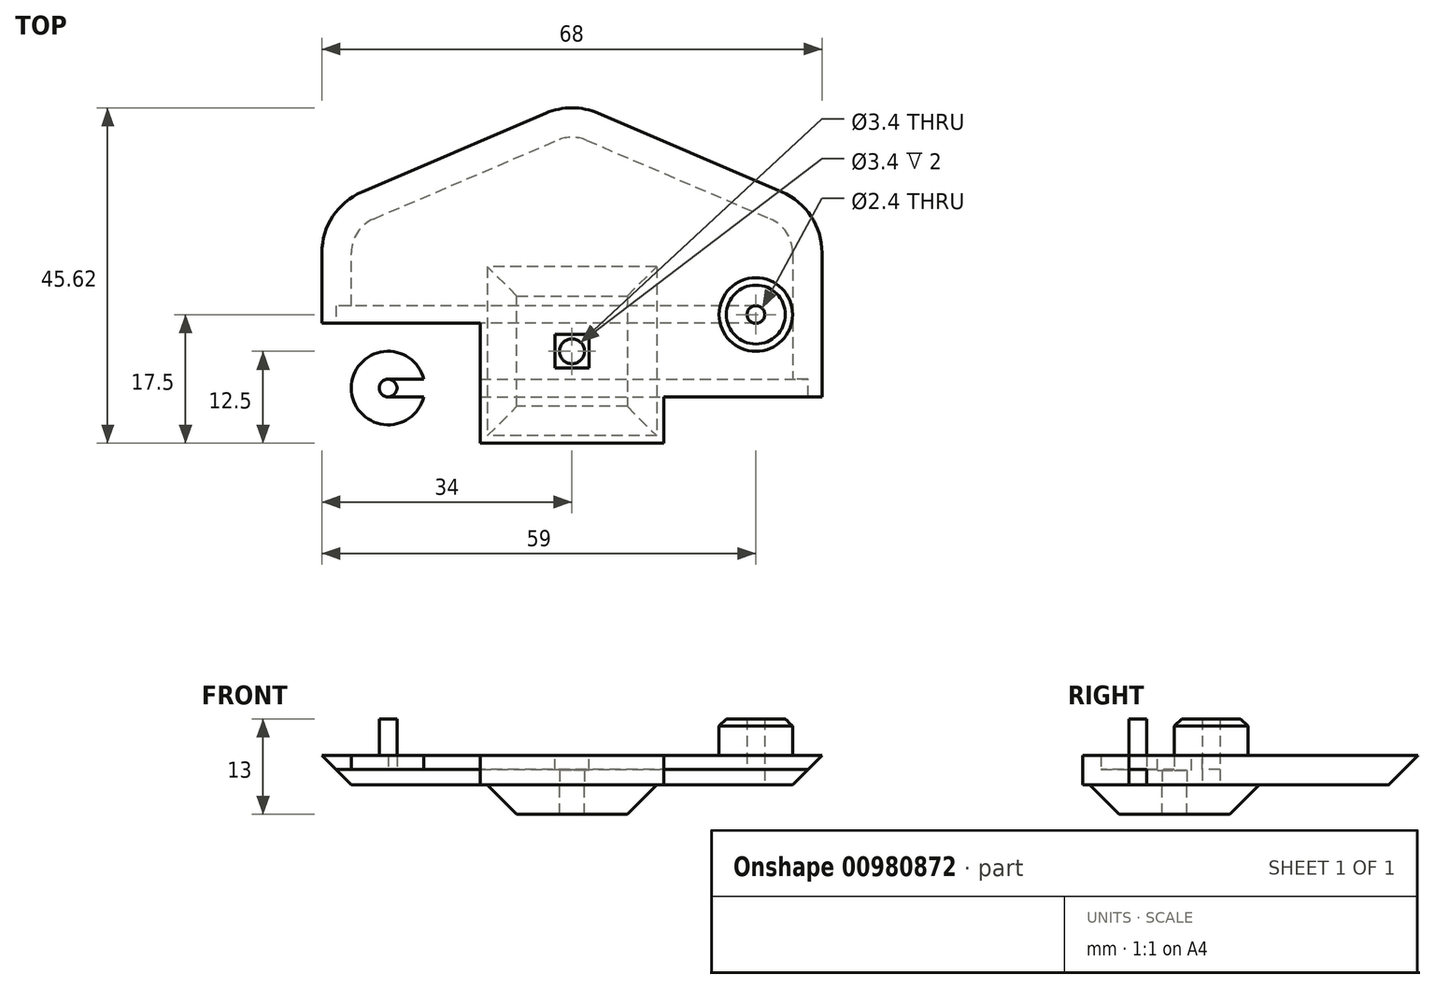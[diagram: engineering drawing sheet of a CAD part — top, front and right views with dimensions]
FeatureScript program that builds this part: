
annotation { "Feature Type Name" : "Feature", "Feature Type Description" : "" }
export const myFeature = defineFeature(function(context is Context, id is Id, definition is map)
    precondition{}
    {
        {
            var Q0;
            Q0=qCreatedBy(makeId("Top.planeOp"),FACE);
            var sketch = newSketch(context, id + "F0", { "sketchPlane" : qUnion([Q0])});
            skLineSegment(sketch, "E0.bottom", {"start": v(35, 35) * mm, "end": v(-35, 35) * mm, "construction": true});
            skLineSegment(sketch, "E0.left", {"start": v(35, 35) * mm, "end": v(35, 20) * mm, "construction": true});
            skLineSegment(sketch, "E0.right", {"start": v(-35, 35) * mm, "end": v(-35, 20) * mm, "construction": true});
            skPoint(sketch, "E0.middle", {"position": v(0, 0) * mm});
            skCircle(sketch, "E1", {"center": v(25, 5) * mm, "radius": 5 * mm});
            skLineSegment(sketch, "E2", {"start": v(35, 20) * mm, "end": v(-35, 20) * mm, "construction": true});
            skLineSegment(sketch, "E3", {"start": v(28.94, 22.6) * mm, "end": v(3.94, 33.31) * mm});
            skLineSegment(sketch, "E4", {"start": v(-3.94, 33.31) * mm, "end": v(-28.94, 22.6) * mm});
            skPoint(sketch, "E5.visualSharp", {"position": v(0, 35) * mm});
            skArc(sketch, "E5.filletArc", {"start": v(3.94, 33.31) * mm, "mid": v(0, 34.12) * mm, "end": v(-3.94, 33.31) * mm});
            skLineSegment(sketch, "E6", {"start": v(35, 13.4) * mm, "end": v(35, 0.5) * mm});
            skLineSegment(sketch, "E7", {"start": v(-35, 13.4) * mm, "end": v(-35, 0.3) * mm});
            skPoint(sketch, "E8.visualSharp", {"position": v(35, 20) * mm});
            skArc(sketch, "E8.filletArc", {"start": v(35, 13.4) * mm, "mid": v(33.35, 18.91) * mm, "end": v(28.94, 22.6) * mm});
            skPoint(sketch, "E9.visualSharp", {"position": v(-35, 20) * mm});
            skArc(sketch, "E9.filletArc", {"start": v(-28.94, 22.6) * mm, "mid": v(-33.35, 18.91) * mm, "end": v(-35, 13.4) * mm});
            skPoint(sketch, "E0.top.end.orphan", {"position": v(-35, -35) * mm});
            skPoint(sketch, "E10.end.orphan", {"position": v(35, -35) * mm});
            skCircle(sketch, "E11.MirrorC", {"center": v(25, 5) * mm, "radius": 1.2 * mm});
            skArc(sketch, "E12.MirrorCS", {"start": v(3.94, -33.31) * mm, "mid": v(0, -34.12) * mm, "end": v(-3.94, -33.31) * mm});
            skArc(sketch, "E13.MirrorCS", {"start": v(-28.94, -22.6) * mm, "mid": v(-33.35, -18.91) * mm, "end": v(-35, -13.4) * mm});
            skPoint(sketch, "E14.MirrorP", {"position": v(-35, -20) * mm});
            skArc(sketch, "E15.MirrorCS", {"start": v(35, -13.4) * mm, "mid": v(33.35, -18.91) * mm, "end": v(28.94, -22.6) * mm});
            skLineSegment(sketch, "E16.MirrorCS", {"start": v(28.94, -22.6) * mm, "end": v(3.94, -33.31) * mm});
            skLineSegment(sketch, "E17.MirrorCS", {"start": v(35, -35) * mm, "end": v(35, -20) * mm, "construction": true});
            skLineSegment(sketch, "E18.MirrorCS", {"start": v(35, -20) * mm, "end": v(-35, -20) * mm, "construction": true});
            skLineSegment(sketch, "E19.MirrorCS", {"start": v(35, -35) * mm, "end": v(-35, -35) * mm, "construction": true});
            skLineSegment(sketch, "E20.MirrorCS", {"start": v(-35, -35) * mm, "end": v(-35, -20) * mm, "construction": true});
            skLineSegment(sketch, "E21.MirrorCS", {"start": v(35, -13.4) * mm, "end": v(35, -0.5) * mm});
            skPoint(sketch, "E22.MirrorP", {"position": v(0, -35) * mm});
            skPoint(sketch, "E23.MirrorP", {"position": v(35, -20) * mm});
            skLineSegment(sketch, "E24.MirrorCS", {"start": v(-3.94, -33.31) * mm, "end": v(-28.94, -22.6) * mm});
            skLineSegment(sketch, "E25.MirrorCS", {"start": v(-35, -13.4) * mm, "end": v(-35, -0.3) * mm});
            skCircle(sketch, "E26.MirrorC", {"center": v(-25, -5) * mm, "radius": 1.2 * mm});
            skCircle(sketch, "E27.MirrorC", {"center": v(-25, -5) * mm, "radius": 5 * mm});
            skLineSegment(sketch, "E28.bottom", {"start": v(12.5, 12.5) * mm, "end": v(-12.5, 12.5) * mm});
            skLineSegment(sketch, "E28.top", {"start": v(12.5, -12.5) * mm, "end": v(-12.5, -12.5) * mm});
            skLineSegment(sketch, "E28.left", {"start": v(12.5, 12.5) * mm, "end": v(12.5, -12.5) * mm});
            skLineSegment(sketch, "E28.right", {"start": v(-12.5, 12.5) * mm, "end": v(-12.5, -12.5) * mm});
            skCircle(sketch, "E29", {"center": v(0, 0) * mm, "radius": 1.7 * mm});
            skLineSegment(sketch, "E30", {"start": v(-35, -0.3) * mm, "end": v(-35, 0.3) * mm});
            skLineSegment(sketch, "E31", {"start": v(35, -0.5) * mm, "end": v(35, 0.5) * mm});
            skLineSegment(sketch, "E32", {"start": v(25, 3.8) * mm, "end": v(-35, 3.8) * mm});
            skPoint(sketch, "E32.endSnap0", {"position": v(-35, 6.85) * mm});
            skLineSegment(sketch, "E33", {"start": v(25, 6.2) * mm, "end": v(-35, 6.2) * mm});
            skLineSegment(sketch, "E34", {"start": v(-25, -6.2) * mm, "end": v(35, -6.2) * mm});
            skLineSegment(sketch, "E35", {"start": v(-25, -3.8) * mm, "end": v(35, -3.8) * mm});
            skSolve(sketch);
        }
        {
            var Q0;
            Q0=makeQuery(id+"F0.imprint","IMPRINT",FACE,{"disambiguationData":[TD([[makeQuery(id+"F0.imprint","IMPRINT",EDGE,{"derivedFrom":sQuery(id+"F0.wireOp",EDGE,"E12.MirrorCS")}),-1.0]])]});
            var Q1;
            Q1=makeQuery(id+"F0.imprint","IMPRINT",FACE,{"disambiguationData":[TD([[makeQuery(id+"F0.imprint","IMPRINT",EDGE,{"derivedFrom":sQuery(id+"F0.wireOp",EDGE,"E3")}),1.0]])]});
            var Q2;
            {var subQ0=sQuery(id+"F0.wireOp",EDGE,"E32");var subQ1=sQuery(id+"F0.wireOp",EDGE,"E1");var subQ2=makeQuery(id+"F0.imprint","INTERSECT",VERTEX,{"derivedFrom":[subQ1,subQ0]});Q2=makeQuery(id+"F0.imprint","IMPRINT",FACE,{"disambiguationData":[TD([[makeQuery(id+"F0.imprint","IMPRINT",EDGE,{"disambiguationData":[TD([[subQ2,-1.0]])],"derivedFrom":subQ1}),1.0]])]});}
            var Q3;
            {var subQ0=sQuery(id+"F0.wireOp",EDGE,"E32");var subQ1=sQuery(id+"F0.wireOp",EDGE,"E1");var subQ2=makeQuery(id+"F0.imprint","INTERSECT",VERTEX,{"derivedFrom":[subQ1,subQ0]});Q3=makeQuery(id+"F0.imprint","IMPRINT",FACE,{"disambiguationData":[TD([[makeQuery(id+"F0.imprint","IMPRINT",EDGE,{"disambiguationData":[TD([[subQ2,1.0]])],"derivedFrom":subQ1}),1.0]])]});}
            var Q4;
            {var subQ0=sQuery(id+"F0.wireOp",EDGE,"E32");var subQ1=sQuery(id+"F0.wireOp",EDGE,"E1");var subQ2=makeQuery(id+"F0.imprint","INTERSECT",VERTEX,{"derivedFrom":[subQ1,subQ0]});Q4=makeQuery(id+"F0.imprint","IMPRINT",FACE,{"disambiguationData":[TD([[makeQuery(id+"F0.imprint","IMPRINT",EDGE,{"disambiguationData":[TD([[subQ2,1.0]])],"derivedFrom":subQ1}),-1.0]])]});}
            var Q5;
            {var subQ0=sQuery(id+"F0.wireOp",EDGE,"E28.bottom");Q5=makeQuery(id+"F0.imprint","IMPRINT",FACE,{"disambiguationData":[TD([[makeQuery(id+"F0.imprint","IMPRINT",EDGE,{"derivedFrom":subQ0}),1.0]])]});}
            var Q6;
            {var subQ0=sQuery(id+"F0.wireOp",EDGE,"E33");var subQ1=sQuery(id+"F0.wireOp",EDGE,"E28.left");var subQ2=makeQuery(id+"F0.imprint","INTERSECT",VERTEX,{"derivedFrom":[subQ1,subQ0]});Q6=makeQuery(id+"F0.imprint","IMPRINT",FACE,{"disambiguationData":[TD([[makeQuery(id+"F0.imprint","IMPRINT",EDGE,{"disambiguationData":[TD([[subQ2,-1.0]])],"derivedFrom":subQ1}),-1.0]])]});}
            var Q7;
            Q7=makeQuery(id+"F0.imprint","IMPRINT",FACE,{"disambiguationData":[TD([[makeQuery(id+"F0.imprint","IMPRINT",EDGE,{"derivedFrom":sQuery(id+"F0.wireOp",EDGE,"E29")}),-1.0]])]});
            var Q8;
            {var subQ0=sQuery(id+"F0.wireOp",EDGE,"E32");var subQ1=sQuery(id+"F0.wireOp",EDGE,"E7");var subQ2=makeQuery(id+"F0.imprint","INTERSECT",VERTEX,{"derivedFrom":[subQ1,subQ0]});Q8=makeQuery(id+"F0.imprint","IMPRINT",FACE,{"disambiguationData":[TD([[makeQuery(id+"F0.imprint","IMPRINT",EDGE,{"disambiguationData":[TD([[subQ2,1.0]])],"derivedFrom":subQ1}),1.0]])]});}
            var Q9;
            {var subQ0=sQuery(id+"F0.wireOp",EDGE,"E34");var subQ1=sQuery(id+"F0.wireOp",EDGE,"E26.MirrorC");var subQ2=makeQuery(id+"F0.imprint","INTERSECT",VERTEX,{"derivedFrom":[subQ1,subQ0]});Q9=makeQuery(id+"F0.imprint","IMPRINT",FACE,{"disambiguationData":[TD([[makeQuery(id+"F0.imprint","IMPRINT",EDGE,{"disambiguationData":[TD([[subQ2,-1.0]])],"derivedFrom":subQ1}),1.0]])]});}
            var Q10;
            {var subQ0=sQuery(id+"F0.wireOp",EDGE,"E34");var subQ1=sQuery(id+"F0.wireOp",EDGE,"E26.MirrorC");var subQ2=makeQuery(id+"F0.imprint","INTERSECT",VERTEX,{"derivedFrom":[subQ1,subQ0]});Q10=makeQuery(id+"F0.imprint","IMPRINT",FACE,{"disambiguationData":[TD([[makeQuery(id+"F0.imprint","IMPRINT",EDGE,{"disambiguationData":[TD([[subQ2,1.0]])],"derivedFrom":subQ1}),1.0]])]});}
            var Q11;
            {var subQ0=sQuery(id+"F0.wireOp",EDGE,"E34");var subQ1=sQuery(id+"F0.wireOp",EDGE,"E21.MirrorCS");var subQ2=makeQuery(id+"F0.imprint","INTERSECT",VERTEX,{"derivedFrom":[subQ1,subQ0]});Q11=makeQuery(id+"F0.imprint","IMPRINT",FACE,{"disambiguationData":[TD([[makeQuery(id+"F0.imprint","IMPRINT",EDGE,{"disambiguationData":[TD([[subQ2,-1.0]])],"derivedFrom":subQ1}),1.0]])]});}
            var Q12;
            {var subQ0=sQuery(id+"F0.wireOp",EDGE,"E28.top");Q12=makeQuery(id+"F0.imprint","IMPRINT",FACE,{"disambiguationData":[TD([[makeQuery(id+"F0.imprint","IMPRINT",EDGE,{"derivedFrom":subQ0}),-1.0]])]});}
            var Q13;
            {var subQ0=sQuery(id+"F0.wireOp",EDGE,"E34");var subQ1=sQuery(id+"F0.wireOp",EDGE,"E27.MirrorC");var subQ2=makeQuery(id+"F0.imprint","INTERSECT",VERTEX,{"derivedFrom":[subQ1,subQ0]});Q13=makeQuery(id+"F0.imprint","IMPRINT",FACE,{"disambiguationData":[TD([[makeQuery(id+"F0.imprint","IMPRINT",EDGE,{"disambiguationData":[TD([[subQ2,1.0]])],"derivedFrom":subQ1}),1.0]])]});}
            var Q14;
            {var subQ0=sQuery(id+"F0.wireOp",EDGE,"E35");var subQ1=sQuery(id+"F0.wireOp",EDGE,"E28.left");var subQ2=makeQuery(id+"F0.imprint","INTERSECT",VERTEX,{"derivedFrom":[subQ1,subQ0]});Q14=makeQuery(id+"F0.imprint","IMPRINT",FACE,{"disambiguationData":[TD([[makeQuery(id+"F0.imprint","IMPRINT",EDGE,{"disambiguationData":[TD([[subQ2,-1.0]])],"derivedFrom":subQ1}),-1.0]])]});}
            extrude(context, id + "F1", {"entities" : qUnion([Q0, Q1, Q2, Q3, Q4, Q5, Q6, Q7, Q8, Q9, Q10, Q11, Q12, Q13, Q14]), "depth" : 4 * mm, "offsetDistance" : 25 * mm});
        }
        {
            var Q0;
            {var subQ0=sQuery(id+"F0.wireOp",EDGE,"E34");var subQ1=sQuery(id+"F0.wireOp",EDGE,"E26.MirrorC");var subQ2=makeQuery(id+"F0.imprint","INTERSECT",VERTEX,{"derivedFrom":[subQ1,subQ0]});Q0=makeQuery(id+"F0.imprint","IMPRINT",FACE,{"disambiguationData":[TD([[makeQuery(id+"F0.imprint","IMPRINT",EDGE,{"disambiguationData":[TD([[subQ2,-1.0]])],"derivedFrom":subQ1}),1.0]])]});}
            var Q1;
            {var subQ0=sQuery(id+"F0.wireOp",EDGE,"E32");var subQ1=sQuery(id+"F0.wireOp",EDGE,"E1");var subQ2=makeQuery(id+"F0.imprint","INTERSECT",VERTEX,{"derivedFrom":[subQ1,subQ0]});Q1=makeQuery(id+"F0.imprint","IMPRINT",FACE,{"disambiguationData":[TD([[makeQuery(id+"F0.imprint","IMPRINT",EDGE,{"disambiguationData":[TD([[subQ2,-1.0]])],"derivedFrom":subQ1}),1.0]])]});}
            var Q2;
            {var subQ0=sQuery(id+"F0.wireOp",EDGE,"E32");var subQ1=sQuery(id+"F0.wireOp",EDGE,"E1");var subQ2=makeQuery(id+"F0.imprint","INTERSECT",VERTEX,{"derivedFrom":[subQ1,subQ0]});Q2=makeQuery(id+"F0.imprint","IMPRINT",FACE,{"disambiguationData":[TD([[makeQuery(id+"F0.imprint","IMPRINT",EDGE,{"disambiguationData":[TD([[subQ2,1.0]])],"derivedFrom":subQ1}),1.0]])]});}
            var Q3;
            {var subQ0=sQuery(id+"F0.wireOp",EDGE,"E34");var subQ1=sQuery(id+"F0.wireOp",EDGE,"E26.MirrorC");var subQ2=makeQuery(id+"F0.imprint","INTERSECT",VERTEX,{"derivedFrom":[subQ1,subQ0]});Q3=makeQuery(id+"F0.imprint","IMPRINT",FACE,{"disambiguationData":[TD([[makeQuery(id+"F0.imprint","IMPRINT",EDGE,{"disambiguationData":[TD([[subQ2,1.0]])],"derivedFrom":subQ1}),1.0]])]});}
            extrude(context, id + "F2", {"entities" : qUnion([Q0, Q1, Q2, Q3]), "operationType" : NewBodyOperationType.ADD, "depth" : 9 * mm, "offsetDistance" : 25 * mm});
        }
        {
            var Q0;
            {var subQ0=sQuery(id+"F0.wireOp",EDGE,"E34");var subQ1=sQuery(id+"F0.wireOp",EDGE,"E26.MirrorC");var subQ2=makeQuery(id+"F0.imprint","INTERSECT",VERTEX,{"derivedFrom":[subQ1,subQ0]});Q0=makeQuery(id+"F0.imprint","IMPRINT",FACE,{"disambiguationData":[TD([[makeQuery(id+"F0.imprint","IMPRINT",EDGE,{"disambiguationData":[TD([[subQ2,1.0]])],"derivedFrom":subQ1}),1.0]])]});}
            var Q1;
            {var subQ0=sQuery(id+"F0.wireOp",EDGE,"E34");var subQ1=sQuery(id+"F0.wireOp",EDGE,"E27.MirrorC");var subQ2=makeQuery(id+"F0.imprint","INTERSECT",VERTEX,{"derivedFrom":[subQ1,subQ0]});Q1=makeQuery(id+"F0.imprint","IMPRINT",FACE,{"disambiguationData":[TD([[makeQuery(id+"F0.imprint","IMPRINT",EDGE,{"disambiguationData":[TD([[subQ2,1.0]])],"derivedFrom":subQ1}),1.0]])]});}
            var Q2;
            {var subQ0=sQuery(id+"F0.wireOp",EDGE,"E35");var subQ1=sQuery(id+"F0.wireOp",EDGE,"E28.left");var subQ2=makeQuery(id+"F0.imprint","INTERSECT",VERTEX,{"derivedFrom":[subQ1,subQ0]});Q2=makeQuery(id+"F0.imprint","IMPRINT",FACE,{"disambiguationData":[TD([[makeQuery(id+"F0.imprint","IMPRINT",EDGE,{"disambiguationData":[TD([[subQ2,-1.0]])],"derivedFrom":subQ1}),-1.0]])]});}
            var Q3;
            {var subQ0=sQuery(id+"F0.wireOp",EDGE,"E34");var subQ1=sQuery(id+"F0.wireOp",EDGE,"E21.MirrorCS");var subQ2=makeQuery(id+"F0.imprint","INTERSECT",VERTEX,{"derivedFrom":[subQ1,subQ0]});Q3=makeQuery(id+"F0.imprint","IMPRINT",FACE,{"disambiguationData":[TD([[makeQuery(id+"F0.imprint","IMPRINT",EDGE,{"disambiguationData":[TD([[subQ2,-1.0]])],"derivedFrom":subQ1}),1.0]])]});}
            var Q4;
            {var subQ0=sQuery(id+"F0.wireOp",EDGE,"E32");var subQ1=sQuery(id+"F0.wireOp",EDGE,"E1");var subQ2=makeQuery(id+"F0.imprint","INTERSECT",VERTEX,{"derivedFrom":[subQ1,subQ0]});Q4=makeQuery(id+"F0.imprint","IMPRINT",FACE,{"disambiguationData":[TD([[makeQuery(id+"F0.imprint","IMPRINT",EDGE,{"disambiguationData":[TD([[subQ2,1.0]])],"derivedFrom":subQ1}),1.0]])]});}
            var Q5;
            {var subQ0=sQuery(id+"F0.wireOp",EDGE,"E32");var subQ1=sQuery(id+"F0.wireOp",EDGE,"E1");var subQ2=makeQuery(id+"F0.imprint","INTERSECT",VERTEX,{"derivedFrom":[subQ1,subQ0]});Q5=makeQuery(id+"F0.imprint","IMPRINT",FACE,{"disambiguationData":[TD([[makeQuery(id+"F0.imprint","IMPRINT",EDGE,{"disambiguationData":[TD([[subQ2,1.0]])],"derivedFrom":subQ1}),-1.0]])]});}
            var Q6;
            {var subQ0=sQuery(id+"F0.wireOp",EDGE,"E33");var subQ1=sQuery(id+"F0.wireOp",EDGE,"E28.left");var subQ2=makeQuery(id+"F0.imprint","INTERSECT",VERTEX,{"derivedFrom":[subQ1,subQ0]});Q6=makeQuery(id+"F0.imprint","IMPRINT",FACE,{"disambiguationData":[TD([[makeQuery(id+"F0.imprint","IMPRINT",EDGE,{"disambiguationData":[TD([[subQ2,-1.0]])],"derivedFrom":subQ1}),-1.0]])]});}
            var Q7;
            {var subQ0=sQuery(id+"F0.wireOp",EDGE,"E32");var subQ1=sQuery(id+"F0.wireOp",EDGE,"E7");var subQ2=makeQuery(id+"F0.imprint","INTERSECT",VERTEX,{"derivedFrom":[subQ1,subQ0]});Q7=makeQuery(id+"F0.imprint","IMPRINT",FACE,{"disambiguationData":[TD([[makeQuery(id+"F0.imprint","IMPRINT",EDGE,{"disambiguationData":[TD([[subQ2,1.0]])],"derivedFrom":subQ1}),1.0]])]});}
            extrude(context, id + "F3", {"entities" : qUnion([Q0, Q1, Q2, Q3, Q4, Q5, Q6, Q7]), "operationType" : NewBodyOperationType.REMOVE, "depth" : 2.1 * mm, "offsetDistance" : 25 * mm});
        }
        {
            var Q0;
            {var subQ0=sQuery(id+"F0.wireOp",EDGE,"E28.top");Q0=makeQuery(id+"F0.imprint","IMPRINT",FACE,{"disambiguationData":[TD([[makeQuery(id+"F0.imprint","IMPRINT",EDGE,{"derivedFrom":subQ0}),-1.0]])]});}
            var Q1;
            {var subQ0=sQuery(id+"F0.wireOp",EDGE,"E35");var subQ1=sQuery(id+"F0.wireOp",EDGE,"E28.left");var subQ2=makeQuery(id+"F0.imprint","INTERSECT",VERTEX,{"derivedFrom":[subQ1,subQ0]});Q1=makeQuery(id+"F0.imprint","IMPRINT",FACE,{"disambiguationData":[TD([[makeQuery(id+"F0.imprint","IMPRINT",EDGE,{"disambiguationData":[TD([[subQ2,-1.0]])],"derivedFrom":subQ1}),-1.0]])]});}
            var Q2;
            Q2=makeQuery(id+"F0.imprint","IMPRINT",FACE,{"disambiguationData":[TD([[makeQuery(id+"F0.imprint","IMPRINT",EDGE,{"derivedFrom":sQuery(id+"F0.wireOp",EDGE,"E29")}),-1.0]])]});
            var Q3;
            {var subQ0=sQuery(id+"F0.wireOp",EDGE,"E33");var subQ1=sQuery(id+"F0.wireOp",EDGE,"E28.left");var subQ2=makeQuery(id+"F0.imprint","INTERSECT",VERTEX,{"derivedFrom":[subQ1,subQ0]});Q3=makeQuery(id+"F0.imprint","IMPRINT",FACE,{"disambiguationData":[TD([[makeQuery(id+"F0.imprint","IMPRINT",EDGE,{"disambiguationData":[TD([[subQ2,-1.0]])],"derivedFrom":subQ1}),-1.0]])]});}
            var Q4;
            {var subQ0=sQuery(id+"F0.wireOp",EDGE,"E28.bottom");Q4=makeQuery(id+"F0.imprint","IMPRINT",FACE,{"disambiguationData":[TD([[makeQuery(id+"F0.imprint","IMPRINT",EDGE,{"derivedFrom":subQ0}),1.0]])]});}
            extrude(context, id + "F4", {"entities" : qUnion([Q0, Q1, Q2, Q3, Q4]), "oppositeDirection" : true, "depth" : 4 * mm, "offsetDistance" : 25 * mm});
        }
        {
            var Q0;
            Q0=makeQuery(id+"F4.opExtrude","CAP_EDGE",EDGE,{"disambiguationData":[OSD([sQuery(id+"F0.wireOp",EDGE,"E28.left")])],"isStart":false});
            var Q1;
            Q1=makeQuery(id+"F4.opExtrude","CAP_EDGE",EDGE,{"disambiguationData":[OSD([sQuery(id+"F0.wireOp",EDGE,"E28.top")])],"isStart":false});
            var Q2;
            Q2=makeQuery(id+"F4.opExtrude","CAP_EDGE",EDGE,{"disambiguationData":[OSD([sQuery(id+"F0.wireOp",EDGE,"E28.right")])],"isStart":false});
            var Q3;
            Q3=makeQuery(id+"F4.opExtrude","CAP_EDGE",EDGE,{"disambiguationData":[OSD([sQuery(id+"F0.wireOp",EDGE,"E28.bottom")])],"isStart":false});
            var Q4;
            Q4=makeQuery(id+"F1.opExtrude","CAP_EDGE",EDGE,{"disambiguationData":[OSD([sQuery(id+"F0.wireOp",EDGE,"E15.MirrorCS")])],"isStart":true});
            var Q5;
            Q5=makeQuery(id+"F1.opExtrude","CAP_EDGE",EDGE,{"disambiguationData":[OSD([sQuery(id+"F0.wireOp",EDGE,"E4")])],"isStart":true});
            chamfer(context, id + "F5", {"entities" : qUnion([Q0, Q1, Q2, Q3, Q4, Q5]), "width" : 5 * mm, "tangentPropagation" : true});
        }
        {
            var Q0;
            Q0=makeQuery(id+"F2.opExtrude","CAP_EDGE",EDGE,{"disambiguationData":[OSD([sQuery(id+"F0.wireOp",EDGE,"E1")])],"isStart":false});
            var Q1;
            Q1=makeQuery(id+"F2.opExtrude","CAP_EDGE",EDGE,{"disambiguationData":[OSD([sQuery(id+"F0.wireOp",EDGE,"E27.MirrorC")])],"isStart":false});
            chamfer(context, id + "F6", {"entities" : qUnion([Q0, Q1]), "width" : 1 * mm, "tangentPropagation" : true});
        }
        {
            var Q0;
            Q0=makeQuery(id+"F1.opExtrude","CAP_FACE",FACE,{"disambiguationData":[OSD([sQuery(id+"F0.wireOp",EDGE,"E3"),sQuery(id+"F0.wireOp",EDGE,"E4"),sQuery(id+"F0.wireOp",EDGE,"E5.filletArc"),sQuery(id+"F0.wireOp",EDGE,"E6"),sQuery(id+"F0.wireOp",EDGE,"E7"),sQuery(id+"F0.wireOp",EDGE,"E8.filletArc"),sQuery(id+"F0.wireOp",EDGE,"E9.filletArc"),sQuery(id+"F0.wireOp",EDGE,"E11.MirrorC"),sQuery(id+"F0.wireOp",EDGE,"E12.MirrorCS"),sQuery(id+"F0.wireOp",EDGE,"E13.MirrorCS"),sQuery(id+"F0.wireOp",EDGE,"E15.MirrorCS"),sQuery(id+"F0.wireOp",EDGE,"E16.MirrorCS"),sQuery(id+"F0.wireOp",EDGE,"E21.MirrorCS"),sQuery(id+"F0.wireOp",EDGE,"E24.MirrorCS"),sQuery(id+"F0.wireOp",EDGE,"E25.MirrorCS"),sQuery(id+"F0.wireOp",EDGE,"E26.MirrorC"),sQuery(id+"F0.wireOp",EDGE,"E29"),sQuery(id+"F0.wireOp",EDGE,"E30"),sQuery(id+"F0.wireOp",EDGE,"E31")])],"isStart":false});
            var sketch = newSketch(context, id + "F7", { "sketchPlane" : qUnion([Q0])});
            skLineSegment(sketch, "E36.bottom", {"start": v(2.3, -2.3) * mm, "end": v(-2.3, -2.3) * mm});
            skLineSegment(sketch, "E36.top", {"start": v(2.3, 2.3) * mm, "end": v(-2.3, 2.3) * mm});
            skLineSegment(sketch, "E36.left", {"start": v(2.3, -2.3) * mm, "end": v(2.3, 2.3) * mm});
            skLineSegment(sketch, "E36.right", {"start": v(-2.3, -2.3) * mm, "end": v(-2.3, 2.3) * mm});
            skPoint(sketch, "E36.middle", {"position": v(0, 0) * mm});
            skSolve(sketch);
        }
        {
            var Q0;
            Q0=makeQuery(id+"F7.imprint","IMPRINT",FACE,{"disambiguationData":[TD([[makeQuery(id+"F7.imprint","IMPRINT",EDGE,{"derivedFrom":sQuery(id+"F7.wireOp",EDGE,"E36.bottom")}),-1.0]])]});
            extrude(context, id + "F8", {"entities" : qUnion([Q0]), "operationType" : NewBodyOperationType.REMOVE, "oppositeDirection" : true, "depth" : 2 * mm, "offsetDistance" : 25 * mm});
        }
    });
